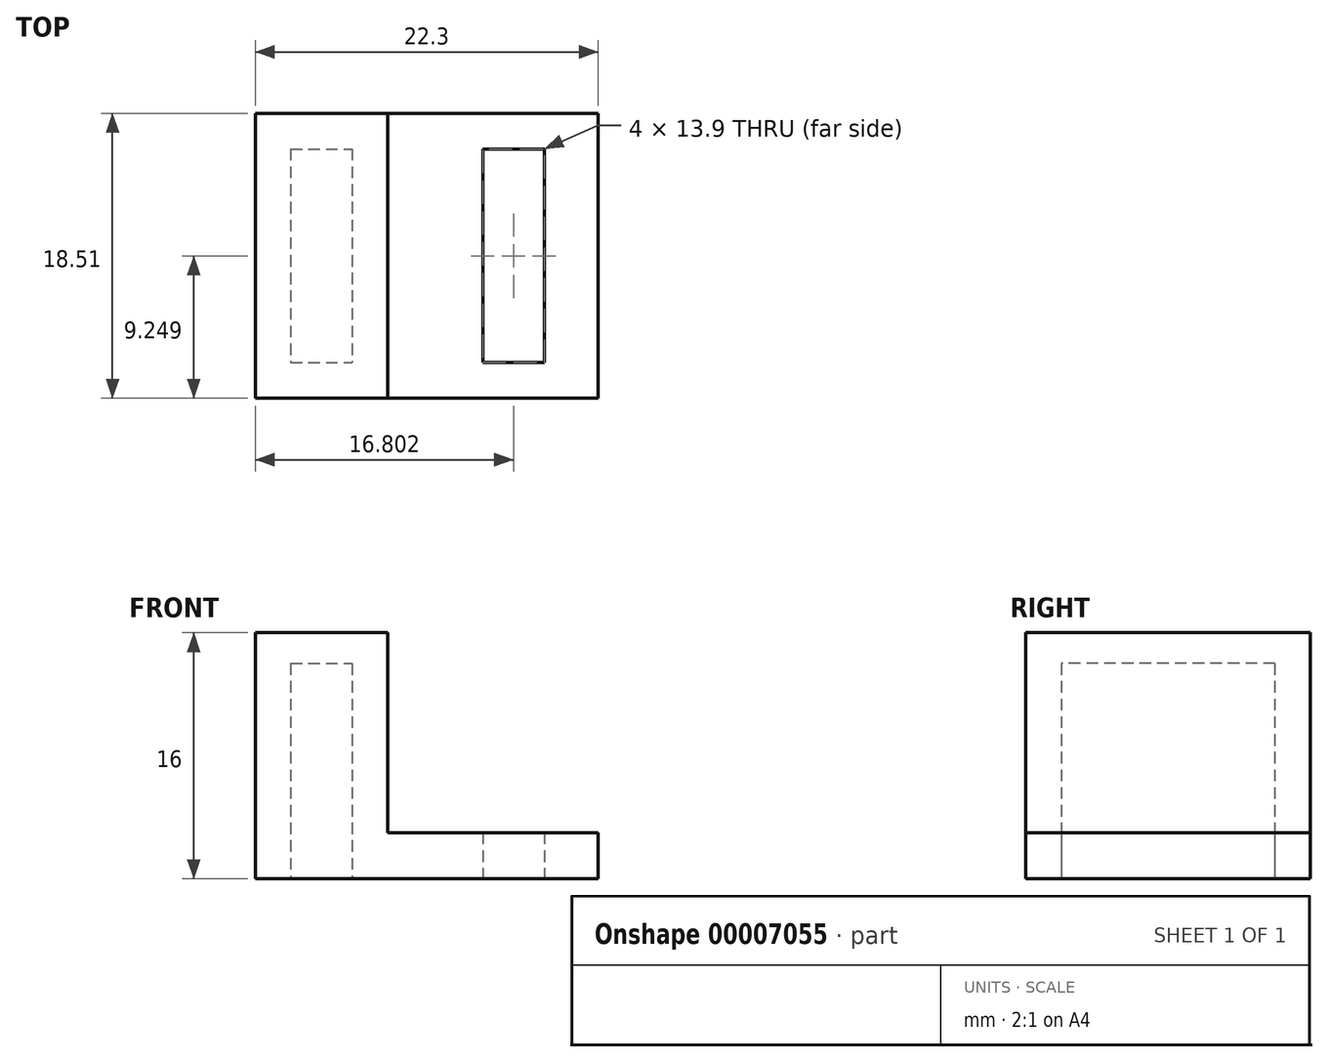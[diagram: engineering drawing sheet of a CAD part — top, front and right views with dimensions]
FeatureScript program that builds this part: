
annotation { "Feature Type Name" : "Feature", "Feature Type Description" : "" }
export const myFeature = defineFeature(function(context is Context, id is Id, definition is map)
    precondition{}
    {
        {
            var Q0;
            Q0=qCreatedBy(makeId("Top.planeOp"),FACE);
            var sketch = newSketch(context, id + "F0", { "sketchPlane" : qUnion([Q0])});
            skLineSegment(sketch, "E0.bottom", {"start": v(-48.96, 30.49) * mm, "end": v(-44.96, 30.49) * mm});
            skLineSegment(sketch, "E0.top", {"start": v(-48.96, 16.59) * mm, "end": v(-44.96, 16.59) * mm});
            skLineSegment(sketch, "E0.left", {"start": v(-48.96, 30.49) * mm, "end": v(-48.96, 16.59) * mm});
            skLineSegment(sketch, "E0.right", {"start": v(-44.96, 30.49) * mm, "end": v(-44.96, 16.59) * mm});
            skLineSegment(sketch, "E1", {"start": v(-44.96, 22.44) * mm, "end": v(-42.66, 22.44) * mm, "construction": true});
            skLineSegment(sketch, "E2", {"start": v(-42.66, 22.44) * mm, "end": v(-42.66, 42.18) * mm, "construction": true});
            skLineSegment(sketch, "E3", {"start": v(-42.66, 42.18) * mm, "end": v(-42.66, 0) * mm, "construction": true});
            skLineSegment(sketch, "E4", {"start": v(-46.96, 30.49) * mm, "end": v(-46.96, 32.79) * mm, "construction": true});
            skLineSegment(sketch, "E5", {"start": v(-46.96, 16.59) * mm, "end": v(-46.96, 14.29) * mm, "construction": true});
            skLineSegment(sketch, "E6", {"start": v(-42.66, 37.35) * mm, "end": v(-28.96, 37.35) * mm, "construction": true});
            skLineSegment(sketch, "E7", {"start": v(-28.96, 37.35) * mm, "end": v(-28.96, 6.43) * mm, "construction": true});
            skLineSegment(sketch, "E8", {"start": v(-46.96, 14.29) * mm, "end": v(-20.97, 14.29) * mm, "construction": true});
            skLineSegment(sketch, "E9", {"start": v(-48.96, 23.54) * mm, "end": v(-51.26, 23.54) * mm, "construction": true});
            skLineSegment(sketch, "E10", {"start": v(-51.26, 23.54) * mm, "end": v(-51.26, 42.06) * mm, "construction": true});
            skLineSegment(sketch, "E11", {"start": v(-51.26, 42.06) * mm, "end": v(-51.26, -3.78) * mm, "construction": true});
            skLineSegment(sketch, "E12", {"start": v(-46.96, 14.29) * mm, "end": v(-58.37, 14.29) * mm, "construction": true});
            skLineSegment(sketch, "E13.bottom", {"start": v(-51.26, 32.8) * mm, "end": v(-28.96, 32.8) * mm});
            skLineSegment(sketch, "E13.top", {"start": v(-51.26, 14.29) * mm, "end": v(-28.96, 14.29) * mm});
            skLineSegment(sketch, "E13.left", {"start": v(-51.26, 32.8) * mm, "end": v(-51.26, 14.29) * mm});
            skLineSegment(sketch, "E13.right", {"start": v(-28.96, 32.8) * mm, "end": v(-28.96, 14.29) * mm});
            skLineSegment(sketch, "E14", {"start": v(-44.96, 30.49) * mm, "end": v(-22.07, 30.49) * mm, "construction": true});
            skLineSegment(sketch, "E15", {"start": v(-44.96, 16.59) * mm, "end": v(-20.97, 16.59) * mm, "construction": true});
            skLineSegment(sketch, "E16", {"start": v(-28.96, 6.43) * mm, "end": v(-32.46, 6.43) * mm, "construction": true});
            skLineSegment(sketch, "E17", {"start": v(-32.46, 6.43) * mm, "end": v(-32.46, 38.78) * mm, "construction": true});
            skPoint(sketch, "E18.firstSnap0", {"position": v(-32.97, 16.59) * mm});
            skLineSegment(sketch, "E18.bottom", {"start": v(-32.46, 16.59) * mm, "end": v(-36.46, 16.59) * mm});
            skLineSegment(sketch, "E18.top", {"start": v(-32.46, 30.49) * mm, "end": v(-36.46, 30.49) * mm});
            skLineSegment(sketch, "E18.left", {"start": v(-32.46, 16.59) * mm, "end": v(-32.46, 30.49) * mm});
            skLineSegment(sketch, "E18.right", {"start": v(-36.46, 16.59) * mm, "end": v(-36.46, 30.49) * mm});
            skLineSegment(sketch, "E19", {"start": v(-42.66, 32.8) * mm, "end": v(-42.66, 14.29) * mm});
            skSolve(sketch);
        }
        {
            var Q0;
            Q0=makeQuery(id+"F0.imprint","IMPRINT",FACE,{"disambiguationData":[TD([[makeQuery(id+"F0.imprint","IMPRINT",EDGE,{"derivedFrom":sQuery(id+"F0.wireOp",EDGE,"E0.bottom")}),1.0]])]});
            extrude(context, id + "F1", {"entities" : qUnion([Q0]), "depth" : 14 * mm});
        }
        {
            var Q0;
            {var subQ0=sQuery(id+"F0.wireOp",EDGE,"E13.right");Q0=makeQuery(id+"F0.imprint","IMPRINT",FACE,{"disambiguationData":[TD([[makeQuery(id+"F0.imprint","IMPRINT",EDGE,{"derivedFrom":subQ0}),-1.0]])]});}
            extrude(context, id + "F2", {"entities" : qUnion([Q0]), "operationType" : NewBodyOperationType.ADD, "depth" : 3 * mm});
        }
        {
            var Q0;
            Q0=makeQuery(id+"F1.opExtrude","CAP_FACE",FACE,{"disambiguationData":[OSD([sQuery(id+"F0.wireOp",EDGE,"E0.bottom"),sQuery(id+"F0.wireOp",EDGE,"E0.top"),sQuery(id+"F0.wireOp",EDGE,"E0.left"),sQuery(id+"F0.wireOp",EDGE,"E0.right"),sQuery(id+"F0.wireOp",EDGE,"E13.bottom"),sQuery(id+"F0.wireOp",EDGE,"E13.top"),sQuery(id+"F0.wireOp",EDGE,"E13.left"),sQuery(id+"F0.wireOp",EDGE,"E19")])],"isStart":false});
            var sketch = newSketch(context, id + "F3", { "sketchPlane" : qUnion([Q0])});
            skLineSegment(sketch, "E20.bottom", {"start": v(-51.26, 32.8) * mm, "end": v(-42.66, 32.8) * mm});
            skLineSegment(sketch, "E20.top", {"start": v(-51.26, 14.29) * mm, "end": v(-42.66, 14.29) * mm});
            skLineSegment(sketch, "E20.left", {"start": v(-51.26, 32.8) * mm, "end": v(-51.26, 14.29) * mm});
            skLineSegment(sketch, "E20.right", {"start": v(-42.66, 32.8) * mm, "end": v(-42.66, 14.29) * mm});
            skSolve(sketch);
        }
        {
            var Q0;
            Q0 = qSketchRegion(id + "F3", true);
            extrude(context, id + "F4", {"entities" : qUnion([Q0]), "operationType" : NewBodyOperationType.ADD, "depth" : 2 * mm});
        }
    });
